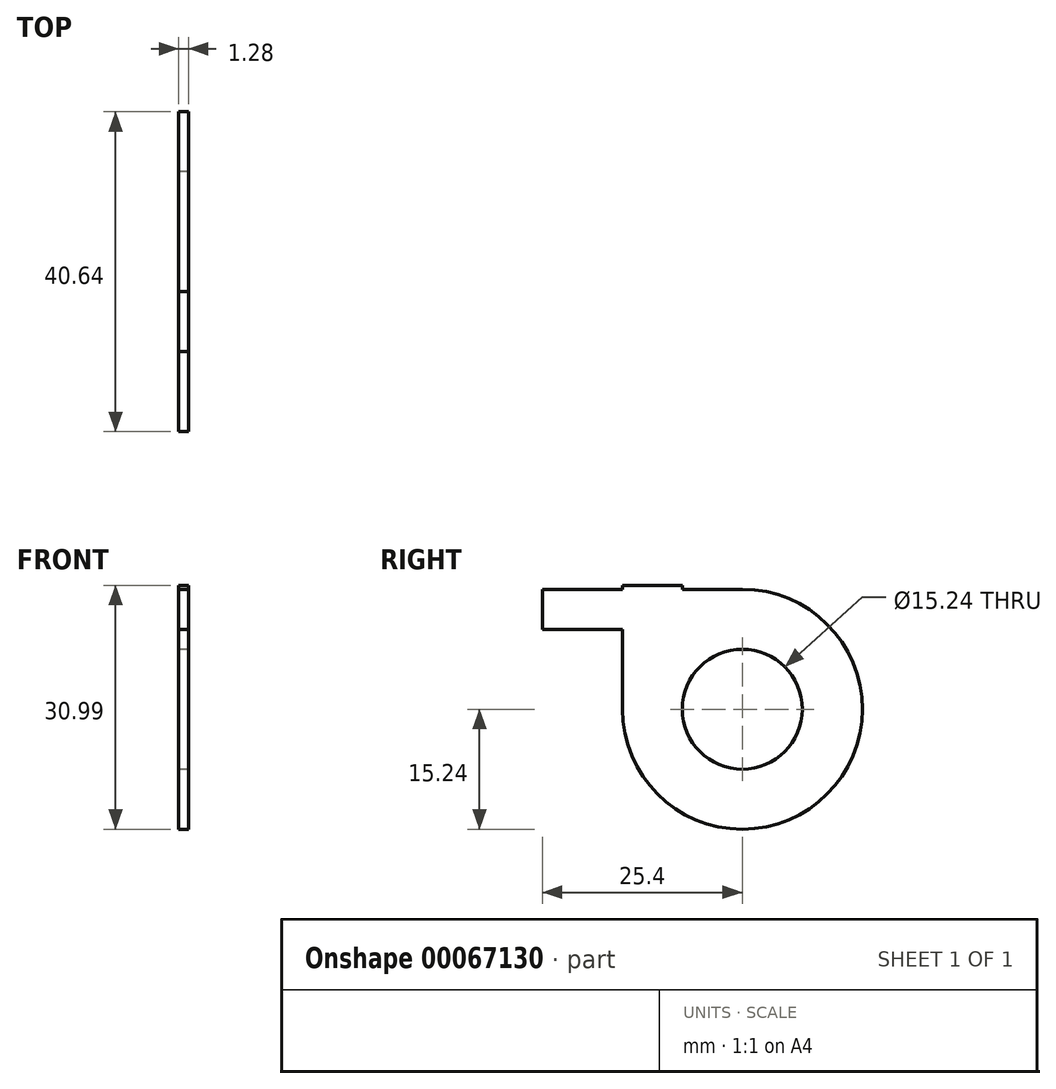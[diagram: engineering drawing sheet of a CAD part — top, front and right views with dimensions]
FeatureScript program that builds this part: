
annotation { "Feature Type Name" : "Feature", "Feature Type Description" : "" }
export const myFeature = defineFeature(function(context is Context, id is Id, definition is map)
    precondition{}
    {
        {
            var Q0;
            Q0=qCreatedBy(makeId("Right.planeOp"),FACE);
            var sketch = newSketch(context, id + "F0", { "sketchPlane" : qUnion([Q0])});
            skLineSegment(sketch, "E0", {"start": v(-25.4, 15.24) * mm, "end": v(0, 15.24) * mm});
            skArc(sketch, "E1", {"start": v(-15.24, 0) * mm, "mid": v(10.78, -10.78) * mm, "end": v(0, 15.24) * mm});
            skLineSegment(sketch, "E2", {"start": v(-25.4, 15.24) * mm, "end": v(-25.4, 10.16) * mm});
            skLineSegment(sketch, "E3", {"start": v(-25.4, 10.16) * mm, "end": v(-15.24, 10.16) * mm});
            skLineSegment(sketch, "E4", {"start": v(-15.24, 10.16) * mm, "end": v(-15.24, 0) * mm});
            skLineSegment(sketch, "E5.top", {"start": v(-15.24, 15.75) * mm, "end": v(-7.62, 15.75) * mm});
            skLineSegment(sketch, "E5.left", {"start": v(-15.24, 15.24) * mm, "end": v(-15.24, 15.75) * mm});
            skLineSegment(sketch, "E5.right", {"start": v(-7.62, 15.24) * mm, "end": v(-7.62, 15.75) * mm});
            skCircle(sketch, "E6", {"center": v(0, 0) * mm, "radius": 7.62 * mm});
            skSolve(sketch);
        }
        {
            var Q0;
            Q0 = qSketchRegion(id + "F0", true);
            extrude(context, id + "F1", {"entities" : qUnion([Q0]), "endBound" : BoundingType.SYMMETRIC, "depth" : 1.27 * mm});
        }
    });
